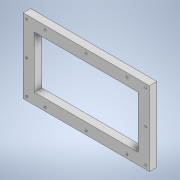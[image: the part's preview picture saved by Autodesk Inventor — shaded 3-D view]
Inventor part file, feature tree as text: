
AUTODESK INVENTOR PART (.ipt)
format: ipt  version: 2022.2 (Build 262287030, 287C)  size: 158,720 bytes
history: native  units: in
note: dims shown in document units (in); Inventor stores cm internally (conversion verified against a paired STEP export)
features: sketch x3, extrude x2, hole x2
ambient origin geometry x8: Origin, YZ Plane, XZ Plane, XY Plane, X Axis, Y Axis, Z Axis, Center Point
bodies: Solid1 (feature_tree)
feature tree (7):
  extrude  "Extrusion1"  Depth=3.937in
  extrude  "Extrusion2"  Depth=5.5118in
  hole  "Hole1"  [1 undecoded]
  hole  "Hole2"  [1 undecoded]
  sketch  "Sketch1"  dims[d0=6.6929in d1=3.937in]
  sketch  "Sketch2"  dims[d2=0.3937in d3=0.0in d4=5.5118in]
  sketch  "Sketch4"  dims[d5=2.7559in d6=0.3937in d7=0.0in d38=0.125in d39=0.2953in d40=0.1476in d41=0.0984in d42=90.0deg d43=0.1969in d44=0.0in d45=0.1969in d53=0.7874in d55=1.9685in d56=0.3937in d58=0.3937in d60=0.7874in d62=6.2992in d63=0.3937in d65=0.3937in d72=1.9685in d73=0.1969in d74=0.1969in d75=3.3465in d78=0.9843in d80=0.1969in d81=0.1969in d82=0.9843in d83=0.7874in d85=6.2992in d86=0.3937in d88=0.3937in d106=0.0984in d107=0.2953in d108=0.1476in d109=0.0984in d110=90.0deg d111=0.1181in d112=0.0in d115=0.1969in d116=0.1969in d117=0.1969in d118=0.7874in d120=3.5433in d121=0.3937in d123=0.3937in d125=1.7717in d131=0.9843in d156=2.2638in d157=0.7874in d159=2.1654in d160=0.7874in d162=3.5433in d158=0.3937in d161=0.1476in d163=0.2953in d164=0.8108in d165=0.0246in d166=0.2953in d167=0.1476in d168=0.0591in d169=0.0984in d170=0.1476in d171=0.5635in d172=0.2953in d173=0.8108in d174=0.0246in d175=0.2953in d176=0.1476in]
note: 2 required parameter values undecoded (feature->parameter linkage not recoverable at this tier; creation-order binding heuristic only, values carry confidence <= 0.55)
